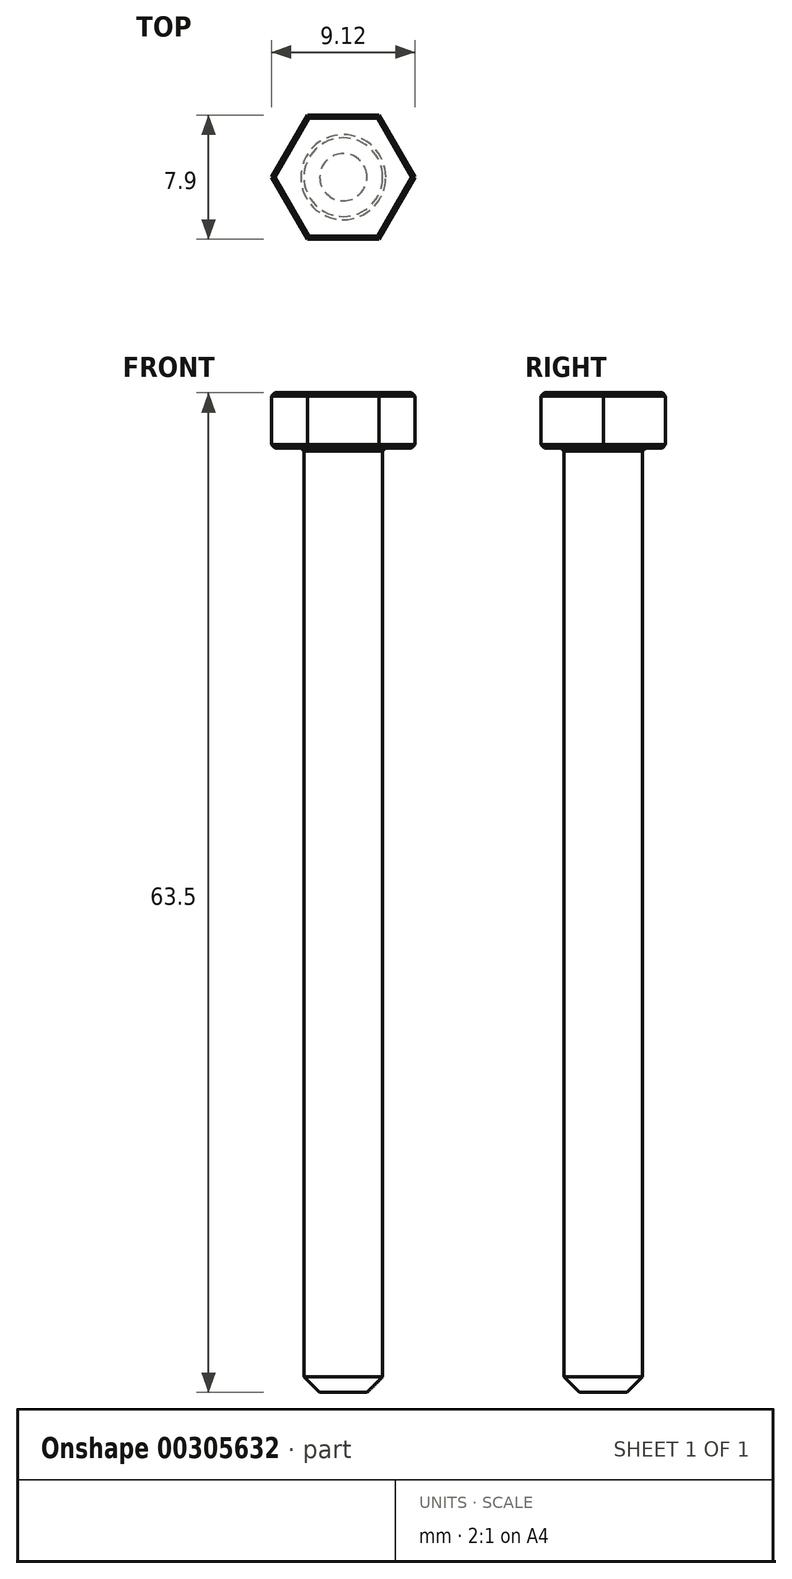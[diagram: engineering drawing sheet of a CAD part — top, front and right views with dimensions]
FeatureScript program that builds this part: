
annotation { "Feature Type Name" : "Feature", "Feature Type Description" : "" }
export const myFeature = defineFeature(function(context is Context, id is Id, definition is map)
    precondition{}
    {
        {
            var Q0;
            Q0=qCreatedBy(makeId("Top.planeOp"),FACE);
            var sketch = newSketch(context, id + "F0", { "sketchPlane" : qUnion([Q0])});
            skCircle(sketch, "E0.cCircle", {"center": v(0, 0) * mm, "radius": 3.95 * mm, "construction": true});
            skLineSegment(sketch, "E0.0", {"start": v(-2.28, 3.95) * mm, "end": v(2.28, 3.95) * mm});
            skLineSegment(sketch, "E0.1", {"start": v(2.28, 3.95) * mm, "end": v(4.56, 0) * mm});
            skLineSegment(sketch, "E0.2", {"start": v(4.56, 0) * mm, "end": v(2.28, -3.95) * mm});
            skLineSegment(sketch, "E0.3", {"start": v(2.28, -3.95) * mm, "end": v(-2.28, -3.95) * mm});
            skLineSegment(sketch, "E0.4", {"start": v(-2.28, -3.95) * mm, "end": v(-4.56, 0) * mm});
            skLineSegment(sketch, "E0.5", {"start": v(-4.56, 0) * mm, "end": v(-2.28, 3.95) * mm});
            skPoint(sketch, "E0.0.midPoint", {"position": v(0, 3.95) * mm});
            skCircle(sketch, "E1", {"center": v(0, 0) * mm, "radius": 2.5 * mm});
            skSolve(sketch);
        }
        {
            var Q0;
            Q0=makeQuery(id+"F0.imprint","IMPRINT",FACE,{"disambiguationData":[TD([[makeQuery(id+"F0.imprint","IMPRINT",EDGE,{"derivedFrom":sQuery(id+"F0.wireOp",EDGE,"E0.0")}),-1.0]])]});
            var Q1;
            Q1=makeQuery(id+"F0.imprint","IMPRINT",FACE,{"disambiguationData":[TD([[makeQuery(id+"F0.imprint","IMPRINT",EDGE,{"derivedFrom":sQuery(id+"F0.wireOp",EDGE,"E1")}),1.0]])]});
            extrude(context, id + "F1", {"entities" : qUnion([Q0, Q1]), "depth" : 3.5 * mm});
        }
        {
            var Q0;
            Q0=makeQuery(id+"F0.imprint","IMPRINT",FACE,{"disambiguationData":[TD([[makeQuery(id+"F0.imprint","IMPRINT",EDGE,{"derivedFrom":sQuery(id+"F0.wireOp",EDGE,"E1")}),1.0]])]});
            extrude(context, id + "F2", {"entities" : qUnion([Q0]), "operationType" : NewBodyOperationType.ADD, "oppositeDirection" : true, "depth" : 60 * mm});
        }
        {
            var Q0;
            Q0=makeQuery(id+"F2.opExtrude","CAP_EDGE",EDGE,{"disambiguationData":[OSD([sQuery(id+"F0.wireOp",EDGE,"E1")])],"isStart":false});
            chamfer(context, id + "F3", {"entities" : qUnion([Q0]), "width" : 1 * mm, "tangentPropagation" : true});
        }
        {
            var Q0;
            Q0=makeQuery(id+"F1.opExtrude","CAP_FACE",FACE,{"disambiguationData":[OSD([sQuery(id+"F0.wireOp",EDGE,"E0.0"),sQuery(id+"F0.wireOp",EDGE,"E0.1"),sQuery(id+"F0.wireOp",EDGE,"E0.2"),sQuery(id+"F0.wireOp",EDGE,"E0.3"),sQuery(id+"F0.wireOp",EDGE,"E0.4"),sQuery(id+"F0.wireOp",EDGE,"E0.5")])],"isStart":false});
            var Q1;
            Q1=makeQuery(id+"F1.opExtrude","CAP_FACE",FACE,{"disambiguationData":[OSD([sQuery(id+"F0.wireOp",EDGE,"E0.0"),sQuery(id+"F0.wireOp",EDGE,"E0.1"),sQuery(id+"F0.wireOp",EDGE,"E0.2"),sQuery(id+"F0.wireOp",EDGE,"E0.3"),sQuery(id+"F0.wireOp",EDGE,"E0.4"),sQuery(id+"F0.wireOp",EDGE,"E0.5")])],"isStart":true});
            chamfer(context, id + "F4", {"entities" : qUnion([Q0, Q1]), "width" : 0.2 * mm, "tangentPropagation" : true});
        }
    });
